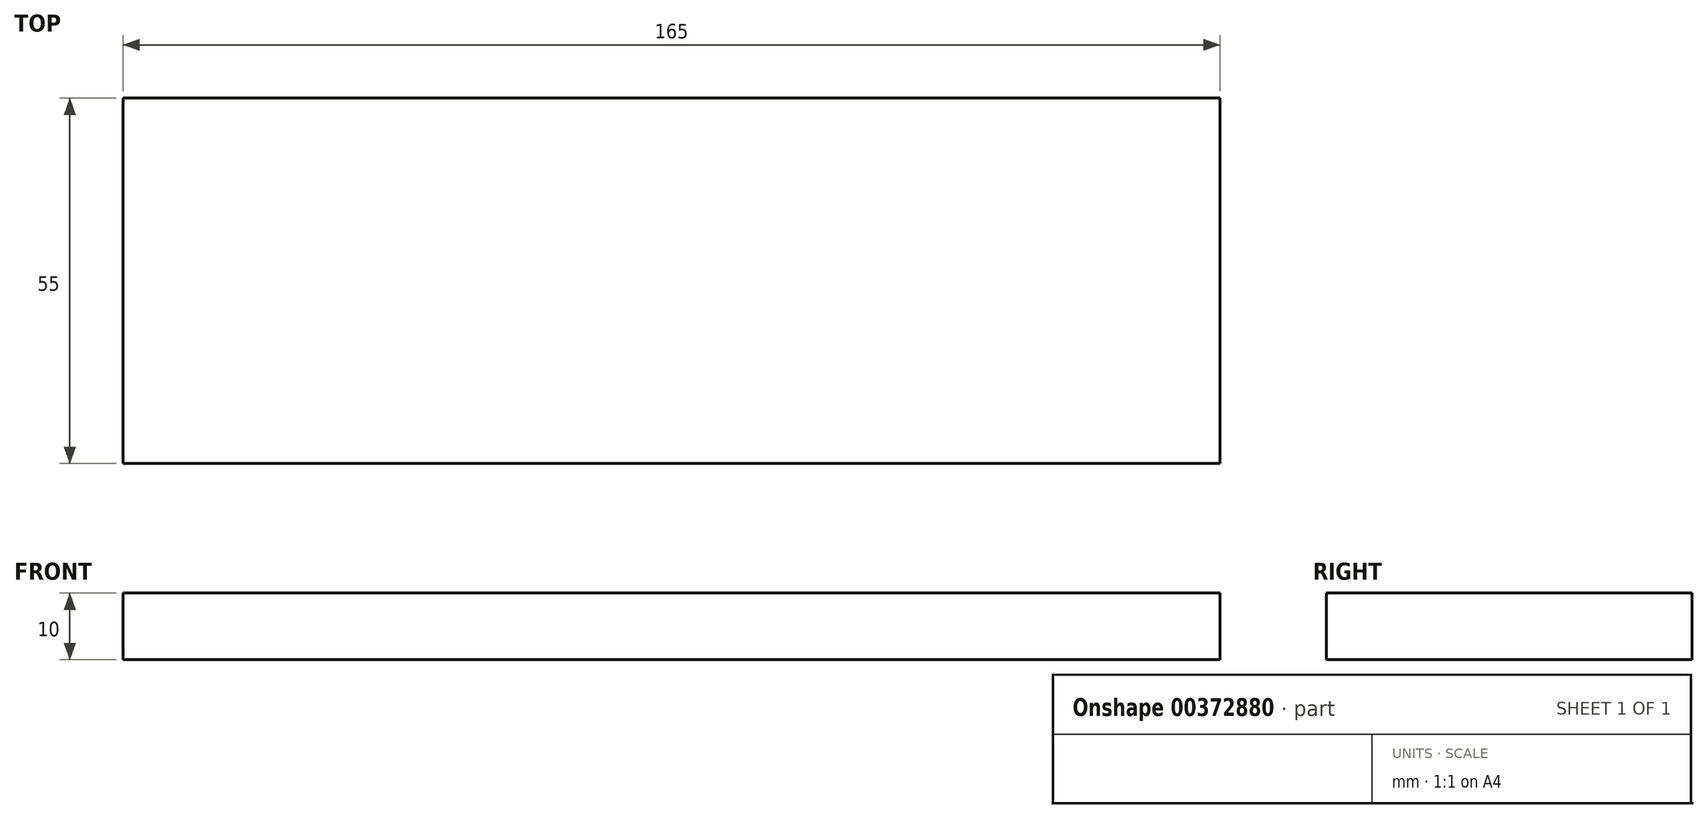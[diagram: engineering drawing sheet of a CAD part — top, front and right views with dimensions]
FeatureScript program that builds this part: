
annotation { "Feature Type Name" : "Feature", "Feature Type Description" : "" }
export const myFeature = defineFeature(function(context is Context, id is Id, definition is map)
    precondition{}
    {
        {
            var Q0;
            Q0=qCreatedBy(makeId("Top.planeOp"),FACE);
            var sketch = newSketch(context, id + "F0", { "sketchPlane" : qUnion([Q0])});
            skLineSegment(sketch, "E0.bottom", {"start": v(-82.5, 27.5) * mm, "end": v(82.5, 27.5) * mm});
            skLineSegment(sketch, "E0.top", {"start": v(-82.5, -27.5) * mm, "end": v(82.5, -27.5) * mm});
            skLineSegment(sketch, "E0.left", {"start": v(-82.5, 27.5) * mm, "end": v(-82.5, -27.5) * mm});
            skLineSegment(sketch, "E0.right", {"start": v(82.5, 27.5) * mm, "end": v(82.5, -27.5) * mm});
            skLineSegment(sketch, "E1", {"start": v(-82.5, 27.5) * mm, "end": v(82.5, -27.5) * mm, "construction": true});
            skSolve(sketch);
        }
        {
            var Q0;
            Q0 = qSketchRegion(id + "F0", true);
            extrude(context, id + "F1", {"entities" : qUnion([Q0]), "depth" : 10 * mm, "offsetDistance" : 25 * mm});
        }
    });
